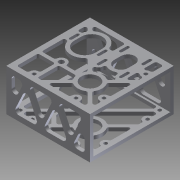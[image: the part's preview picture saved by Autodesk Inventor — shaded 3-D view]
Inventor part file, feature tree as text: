
AUTODESK INVENTOR PART (.ipt)
format: ipt  version: 2012 (Build 160160000, 160)  size: 865,280 bytes
history: native  units: in
note: dims shown in document units (in); Inventor stores cm internally (conversion verified against a paired STEP export)
features: extrude x7, sketch x5, fillet x3, projected_geometry x1
ambient origin geometry x8: Origin, YZ Plane, XZ Plane, XY Plane, X Axis, Y Axis, Z Axis, Center Point
bodies: Solid1 (feature_tree)
feature tree (16):
  extrude  "Extrusion1"  Depth=0.1875in
  sketch  "Sketch2"  dims[d4=0.25in d5=0.25in d6=6.0in d7=0.0in]
  extrude  "Extrusion2"  Depth=6.0in TaperAngle=0.0deg
  extrude  "Extrusion3"  Depth=1.25in
  extrude  "Extrusion4"  Depth=1.625in
  fillet  "Fillet2"  Radius=0.375in
  sketch  "Sketch6"  dims[d20=0.25in d21=0.125in d22=0.25in d24=0.25in d25=0.125in d27=0.125in d32=0.25in d33=0.0in d35=0.375in d36=0.375in d37=0.375in d38=0.375in d39=0.1719in d40=0.3438in d41=0.3438in d42=0.3438in d43=0.3438in d44=0.125in d46=0.125in d49=0.125in d50=0.125in d51=0.125in d52=0.125in d53=0.125in d54=0.125in d55=0.125in d56=0.125in d57=0.25in d58=0.0in d59=0.1719in d60=0.3438in d61=0.3438in d62=0.3438in d63=0.3438in d64=0.125in d65=0.125in d66=0.125in d67=0.125in d68=0.125in d69=0.125in d70=0.125in d71=0.125in d72=0.125in d73=0.125in d74=0.375in d76=0.375in d77=0.375in d78=0.375in d79=0.25in d80=0.0in d81=0.25in d88=0.125in d89=1.25in d90=1.5in d91=0.75in d92=0.5in d94=0.2in d96=0.9in d97=1.0in d98=0.5in d99=0.5in d101=2.0in d102=0.2in d103=0.8in d104=0.8in d105=0.7874in d107=1.6in d108=0.7874in d110=1.6in d114=1.0in d115=1.0in d116=1.625in d117=1.0in d119=0.2in d122=4.5in d123=1.3125in d124=0.366in d126=2.3in d127=0.25in d128=0.0in d129=0.375in d131=4.5in d132=0.125in d153=0.25in d154=0.125in d156=0.375in d157=0.375in d160=0.25in d161=0.125in d162=0.25in d163=0.125in d165=0.875in d166=0.125in d168=0.375in d169=0.25in d170=0.125in d171=1.0in d172=0.25in d177=0.125in d178=0.6in d179=0.25in d180=0.0in d181=0.125in d183=0.25in d185=0.25in d186=0.125in d188=1.5625in d190=1.3125in d191=0.366in d193=0.25in d194=0.125in d197=1.0in d198=1.176in d199=0.1in d200=0.0in d201=0.125in d203=0.25in d204=0.25in d205=0.125in d207=2.1875in d208=2.0312in d211=0.125in d212=0.3in d213=0.5in d214=0.25in d215=0.3125in d220=0.5in d221=1.5in d222=0.25in d224=0.1875in d225=2.3in d226=0.35in d227=0.25in d228=1.5in d229=1.5in d230=0.5821in d231=0.25in d232=1.5in d233=0.125in d234=0.25in d235=2.0in d236=0.25in d237=1.5in d238=0.3125in d239=0.7874in d241=3.0in d242=0.3937in d244=1.0in d246=1.5in d247=0.7874in d249=3.0in d250=0.3937in d252=1.0in d254=0.5in d255=0.25in d256=0.3125in d257=0.25in d258=0.5in d259=0.3125in d260=0.25in d262=0.75in d264=6.0in d267=0.25in d269=3.0in d270=6.0in d272=0.25in]
  fillet  "Fillet3"  Radius=0.875in
  extrude  "Extrusion5"  Depth=0.125in
  extrude  "Extrusion6"  Depth=0.25in
  fillet  "Fillet4"  Radius=0.25in
  extrude  "Extrusion7"  Depth=0.125in
  sketch  "Sketch1"  dims[d1=3.0in d2=0.1875in d3=0.25in]
  sketch  "Sketch4"  dims[d11=2.0312in d13=1.25in]
  sketch  "Sketch5"  dims[d15=2.625in d16=1.625in d18=0.375in d19=0.875in]
  projected_geometry  "Projected Loop1"
